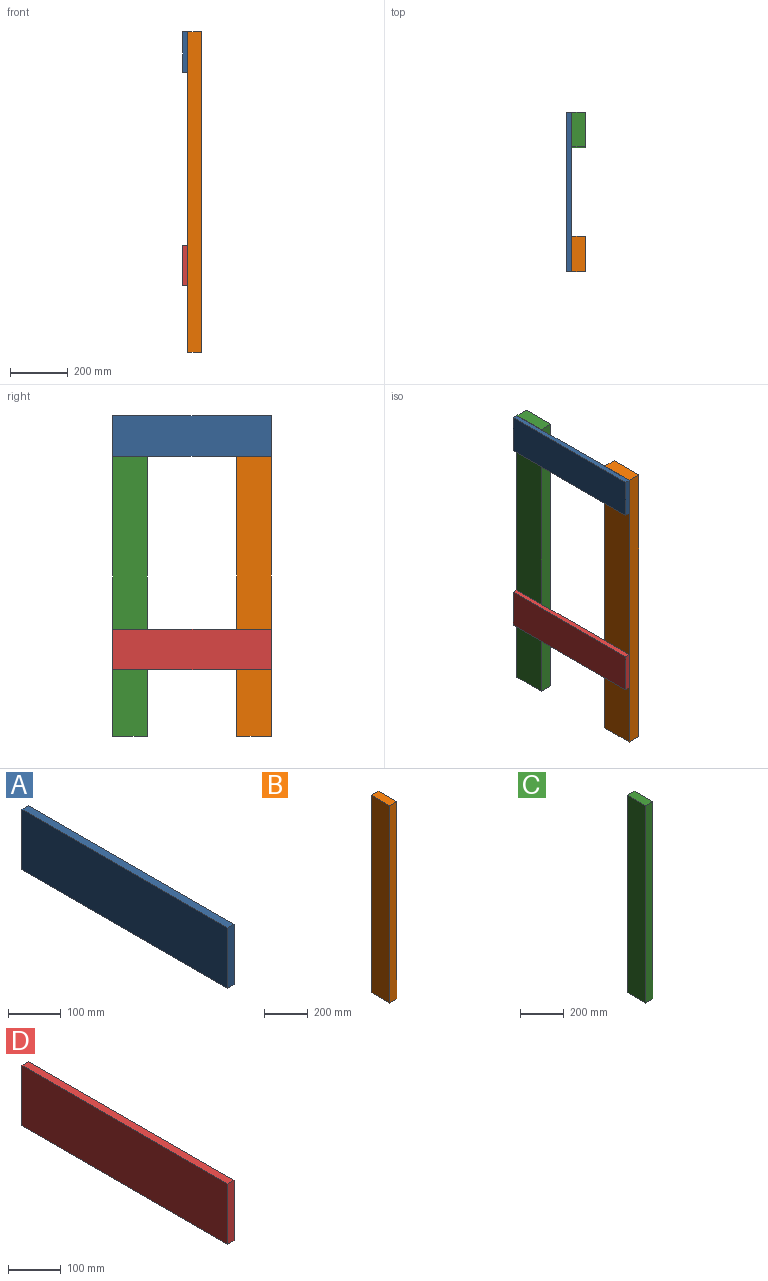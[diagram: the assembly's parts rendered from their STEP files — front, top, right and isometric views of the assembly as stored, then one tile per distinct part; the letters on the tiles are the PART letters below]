
ASSEMBLY  parts=4 mates=3
PART A: 6 faces, bbox 18x550x140 mm
  f0: plane 550x18mm, normal (0,0,-1), area 9900mm2, adj f1,f3,f4,f5
  f1: plane 140x18mm, normal (0,1,0), area 2520mm2, adj f0,f2,f4,f5
  f2: plane 550x18mm, normal (0,0,1), area 9900mm2, adj f1,f3,f4,f5
  f3: plane 140x18mm, normal (0,-1,0), area 2520mm2, adj f0,f2,f4,f5
  f4: plane 550x140mm, normal (1,0,0), area 77000mm2, adj f0,f1,f2,f3
  f5: plane 550x140mm, normal (-1,0,0), area 77000mm2, adj f0,f1,f2,f3
PART B: 6 faces, bbox 47x120x1110 mm
  f0: plane 1110x120mm, normal (-1,0,0), area 133200mm2, adj f1,f3,f4,f5
  f1: plane 1110x47mm, normal (0,-1,0), area 52170mm2, adj f0,f2,f4,f5
  f2: plane 1110x120mm, normal (1,0,0), area 133200mm2, adj f1,f3,f4,f5
  f3: plane 1110x47mm, normal (0,1,0), area 52170mm2, adj f0,f2,f4,f5
  f4: plane 120x47mm, normal (0,0,1), area 5640mm2, adj f0,f1,f2,f3
  f5: plane 120x47mm, normal (0,0,-1), area 5640mm2, adj f0,f1,f2,f3
PART C: 6 faces, bbox 47x120x1110 mm
  f0: plane 1110x120mm, normal (-1,0,0), area 133200mm2, adj f1,f3,f4,f5
  f1: plane 1110x47mm, normal (0,-1,0), area 52170mm2, adj f0,f2,f4,f5
  f2: plane 1110x120mm, normal (1,0,0), area 133200mm2, adj f1,f3,f4,f5
  f3: plane 1110x47mm, normal (0,1,0), area 52170mm2, adj f0,f2,f4,f5
  f4: plane 120x47mm, normal (0,0,1), area 5640mm2, adj f0,f1,f2,f3
  f5: plane 120x47mm, normal (0,0,-1), area 5640mm2, adj f0,f1,f2,f3
PART D: 6 faces, bbox 18x550x140 mm
  f0: plane 140x18mm, normal (0,1,0), area 2520mm2, adj f1,f3,f4,f5
  f1: plane 550x18mm, normal (0,0,1), area 9900mm2, adj f0,f2,f4,f5
  f2: plane 140x18mm, normal (0,-1,0), area 2520mm2, adj f1,f3,f4,f5
  f3: plane 550x18mm, normal (0,0,-1), area 9900mm2, adj f0,f2,f4,f5
  f4: plane 550x140mm, normal (1,0,0), area 77000mm2, adj f0,f1,f2,f3
  f5: plane 550x140mm, normal (-1,0,0), area 77000mm2, adj f0,f1,f2,f3
PLACE A t=(-182.48,-243.09,33.58)mm
PLACE B rot(axis=(0.9,-0.43,-0.08),0deg) t=(-117.48,-243.09,33.58)mm
PLACE C rot(axis=(0.9,-0.43,-0.08),0deg) t=(-117.48,-243.09,33.58)mm
PLACE D rot(axis=(0.9,-0.43,-0.08),0deg) t=(-182.48,-243.09,33.58)mm
MATE fastened A.f4 <-> B.f0  axis (1,0,0) through (-117.48,-243.09,1143.58)mm
MATE fastened A.f5 <-> D.f5  axis (-1,0,0) through (-135.48,31.91,1003.58)mm
MATE fastened C.f0 <-> A.f4  axis (-1,0,0) through (-117.48,306.91,1143.58)mm
